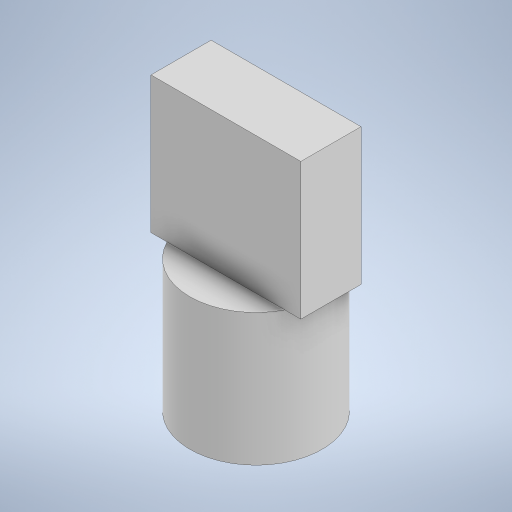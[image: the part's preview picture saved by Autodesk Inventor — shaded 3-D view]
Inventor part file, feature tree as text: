
AUTODESK INVENTOR PART (.ipt)
format: ipt  version: 2024 (Build 280153000, 153)  size: 222,208 bytes
history: native  units: mm
features: extrude x2, sketch x2, other x1
ambient origin geometry x8: Origin, YZ Plane, XZ Plane, XY Plane, X Axis, Y Axis, Z Axis, Center Point
bodies: Body1 (feature_tree)
feature tree (5):
  other  "솔리드1"
  extrude  "돌출1"  Depth=3.0mm
  extrude  "돌출2"  Depth=3.0mm TaperAngle=0.0deg
  sketch  "스케치2"
  sketch  "스케치3"
